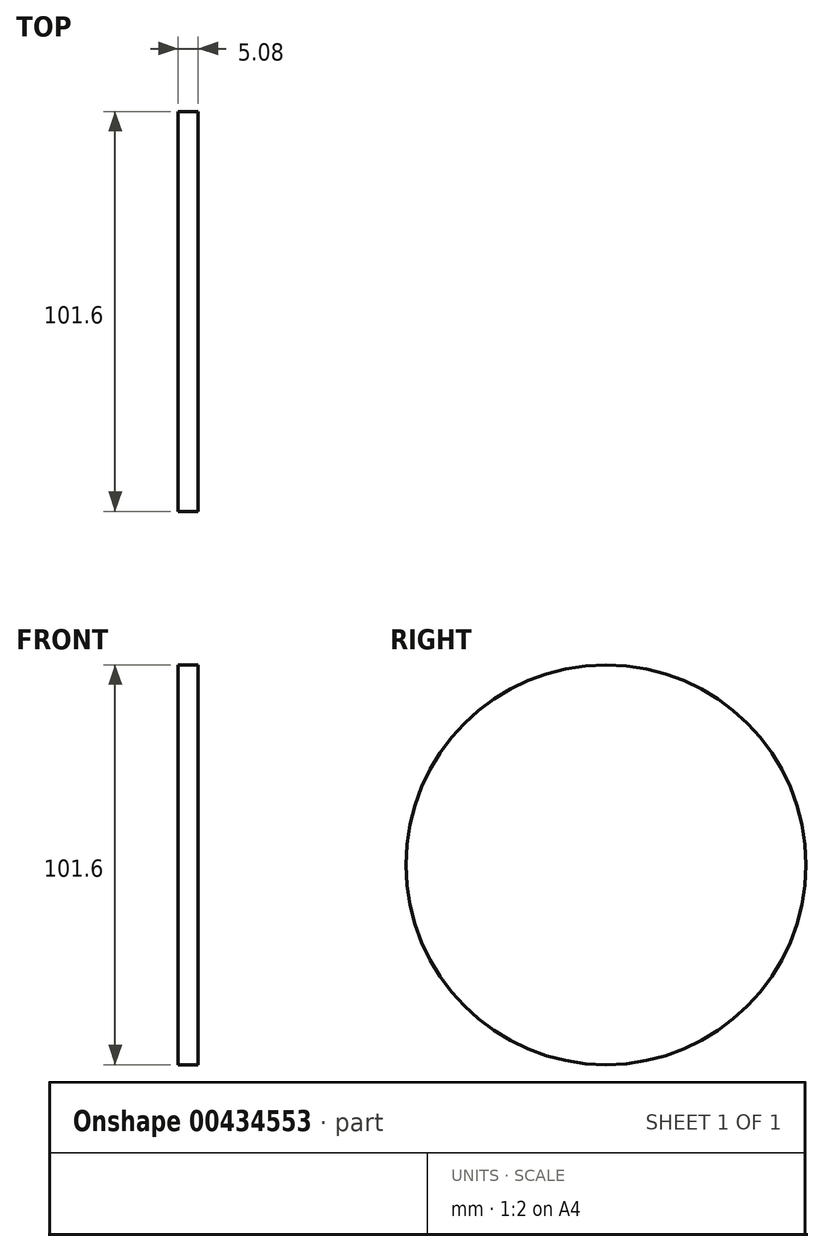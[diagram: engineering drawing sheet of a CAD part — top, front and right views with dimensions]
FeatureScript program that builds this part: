
annotation { "Feature Type Name" : "Feature", "Feature Type Description" : "" }
export const myFeature = defineFeature(function(context is Context, id is Id, definition is map)
    precondition{}
    {
        {
            var Q0;
            Q0=qCreatedBy(makeId("Right.planeOp"),FACE);
            var sketch = newSketch(context, id + "F0", { "sketchPlane" : qUnion([Q0])});
            skCircle(sketch, "E0", {"center": v(0, 0) * mm, "radius": 50.8 * mm});
            skSolve(sketch);
        }
        {
            var Q0;
            Q0 = qSketchRegion(id + "F0", true);
            extrude(context, id + "F1", {"entities" : qUnion([Q0]), "depth" : 5.08 * mm});
        }
    });
